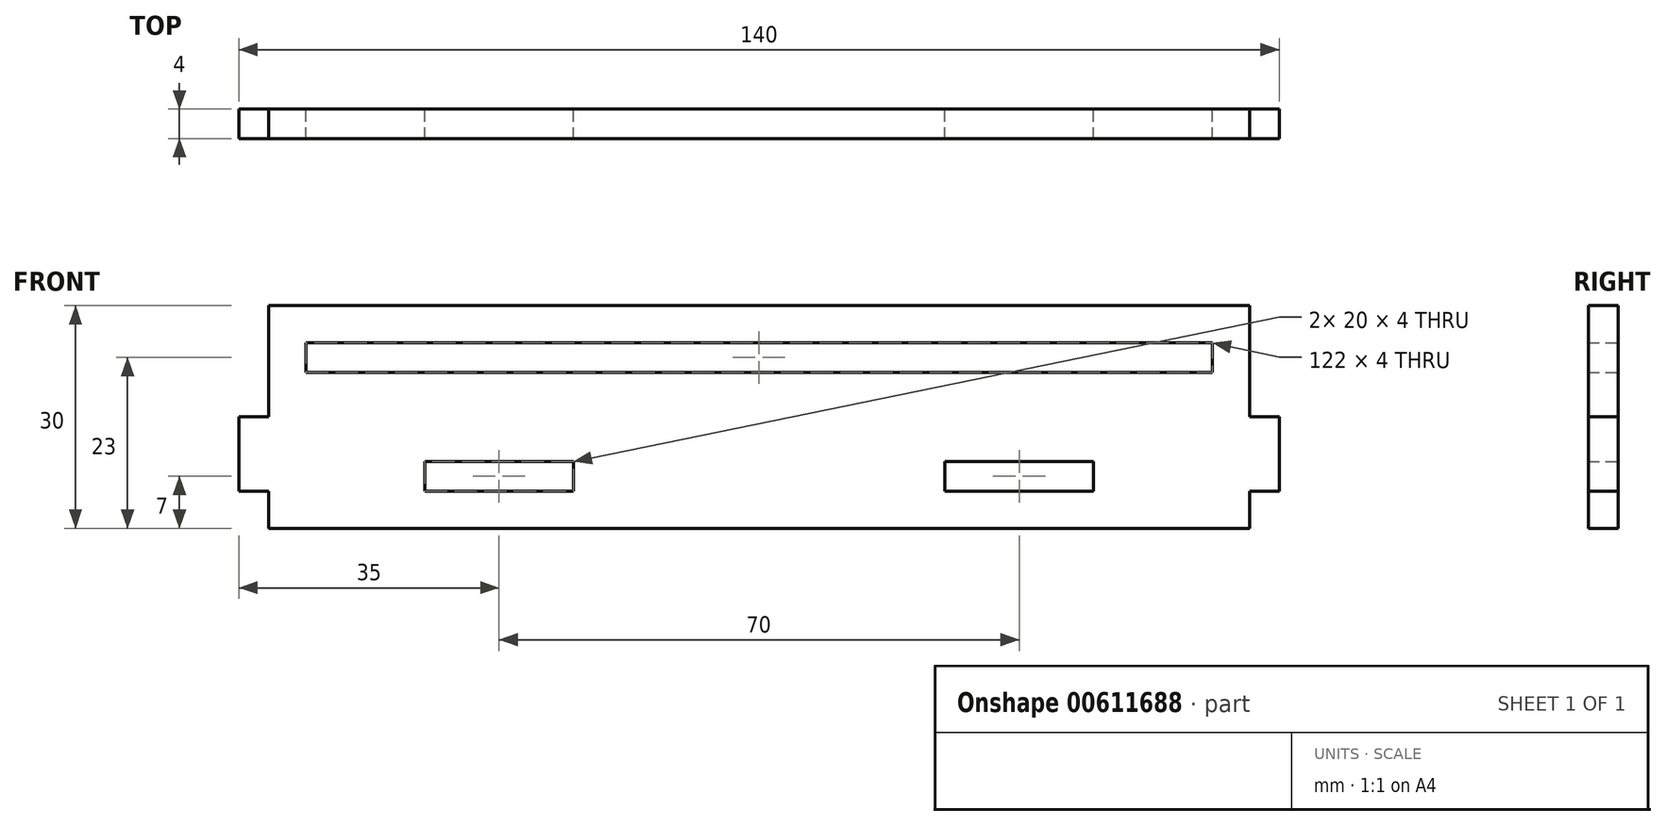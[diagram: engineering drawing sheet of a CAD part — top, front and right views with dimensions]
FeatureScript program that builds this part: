
annotation { "Feature Type Name" : "Feature", "Feature Type Description" : "" }
export const myFeature = defineFeature(function(context is Context, id is Id, definition is map)
    precondition{}
    {
        {
            var Q0;
            Q0=qCreatedBy(makeId("Front.planeOp"),FACE);
            var sketch = newSketch(context, id + "F0", { "sketchPlane" : qUnion([Q0])});
            skLineSegment(sketch, "E0.bottom", {"start": v(66, 15) * mm, "end": v(-66, 15) * mm});
            skLineSegment(sketch, "E0.top", {"start": v(66, -15) * mm, "end": v(-66, -15) * mm});
            skLineSegment(sketch, "E0.left", {"start": v(66, 15) * mm, "end": v(66, 0) * mm});
            skLineSegment(sketch, "E0.right", {"start": v(-66, 15) * mm, "end": v(-66, 0) * mm});
            skPoint(sketch, "E0.middle", {"position": v(0, 0) * mm});
            skLineSegment(sketch, "E1.bottom", {"start": v(-45, -6) * mm, "end": v(-25, -6) * mm});
            skLineSegment(sketch, "E1.top", {"start": v(-45, -10) * mm, "end": v(-25, -10) * mm});
            skLineSegment(sketch, "E1.left", {"start": v(-45, -6) * mm, "end": v(-45, -10) * mm});
            skLineSegment(sketch, "E1.right", {"start": v(-25, -6) * mm, "end": v(-25, -10) * mm});
            skLineSegment(sketch, "E2.MirrorCS", {"start": v(45, -10) * mm, "end": v(25, -10) * mm});
            skLineSegment(sketch, "E3.MirrorCS", {"start": v(45, -6) * mm, "end": v(25, -6) * mm});
            skLineSegment(sketch, "E4.MirrorCS", {"start": v(25, -6) * mm, "end": v(25, -10) * mm});
            skLineSegment(sketch, "E5.MirrorCS", {"start": v(45, -6) * mm, "end": v(45, -10) * mm});
            skLineSegment(sketch, "E6.bottom", {"start": v(-61, 10) * mm, "end": v(61, 10) * mm});
            skLineSegment(sketch, "E6.top", {"start": v(-61, 6) * mm, "end": v(61, 6) * mm});
            skLineSegment(sketch, "E6.left", {"start": v(-61, 10) * mm, "end": v(-61, 6) * mm});
            skLineSegment(sketch, "E6.right", {"start": v(61, 10) * mm, "end": v(61, 6) * mm});
            skLineSegment(sketch, "E7.bottom", {"start": v(-66, 0) * mm, "end": v(-70, 0) * mm});
            skLineSegment(sketch, "E7.top", {"start": v(-66, -10) * mm, "end": v(-70, -10) * mm});
            skLineSegment(sketch, "E7.right", {"start": v(-70, 0) * mm, "end": v(-70, -10) * mm});
            skLineSegment(sketch, "E8.trimOffspring", {"start": v(-66, -10) * mm, "end": v(-66, -15) * mm});
            skLineSegment(sketch, "E9.MirrorCS", {"start": v(66, 0) * mm, "end": v(70, 0) * mm});
            skLineSegment(sketch, "E10.MirrorCS", {"start": v(70, 0) * mm, "end": v(70, -10) * mm});
            skLineSegment(sketch, "E11.MirrorCS", {"start": v(66, -10) * mm, "end": v(70, -10) * mm});
            skLineSegment(sketch, "E12.trimOffspring", {"start": v(66, -10) * mm, "end": v(66, -15) * mm});
            skSolve(sketch);
        }
        {
            var Q0;
            Q0 = qSketchRegion(id + "F0", true);
            extrude(context, id + "F1", {"entities" : qUnion([Q0]), "depth" : 4 * mm, "offsetDistance" : 25 * mm});
        }
    });
